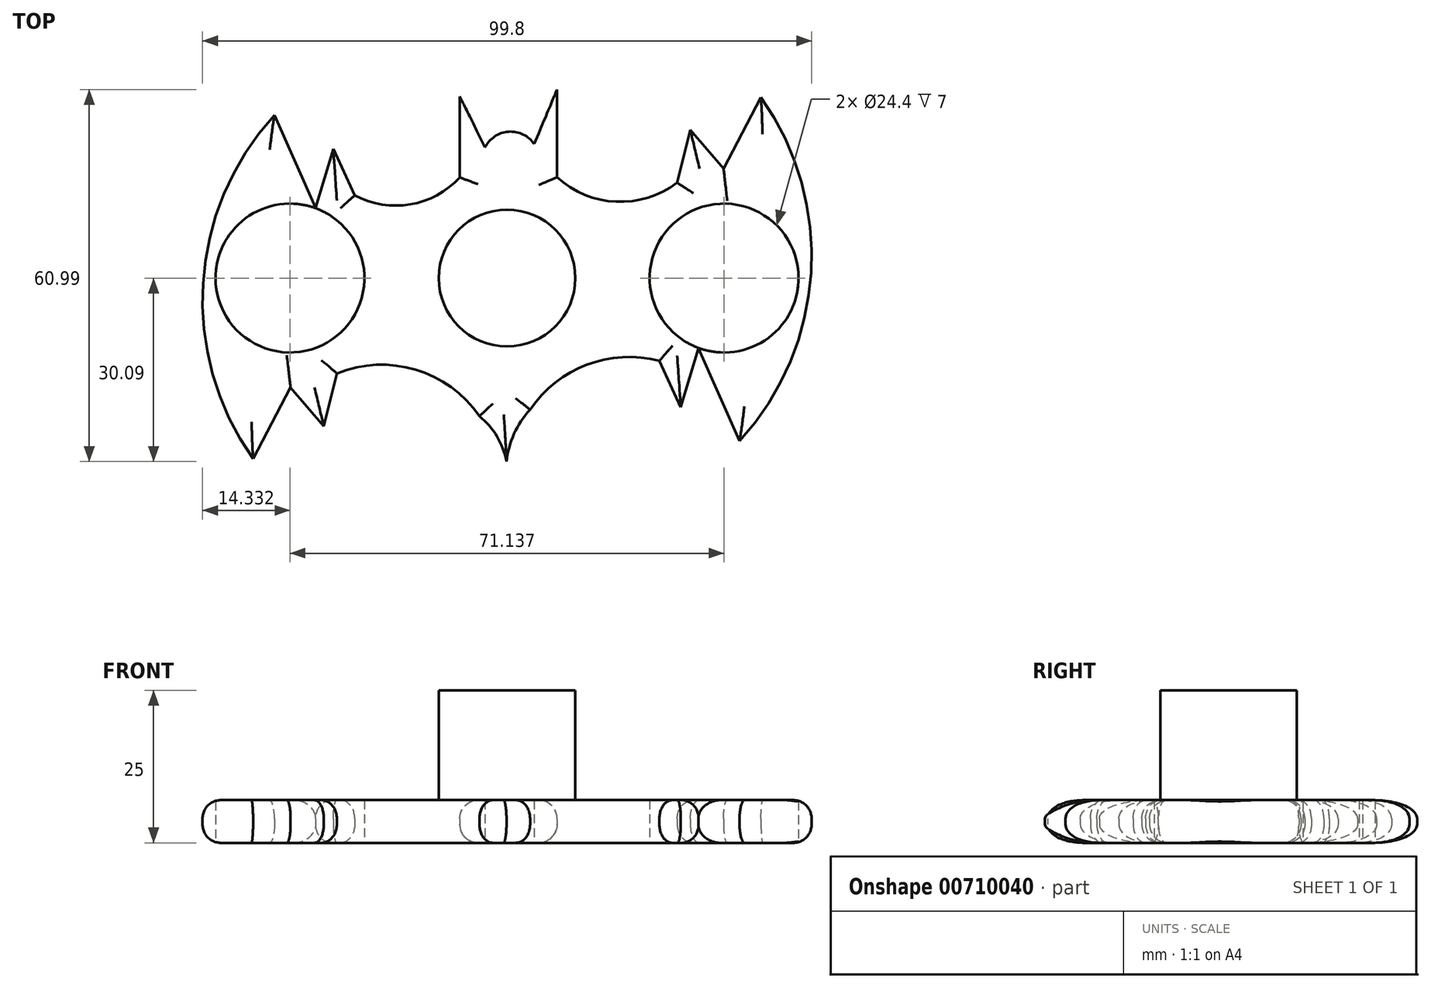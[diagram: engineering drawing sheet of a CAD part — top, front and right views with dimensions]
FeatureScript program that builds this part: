
annotation { "Feature Type Name" : "Feature", "Feature Type Description" : "" }
export const myFeature = defineFeature(function(context is Context, id is Id, definition is map)
    precondition{}
    {
        {
            var Q0;
            Q0=qCreatedBy(makeId("Top.planeOp"),FACE);
            var sketch = newSketch(context, id + "F0", { "sketchPlane" : qUnion([Q0])});
            skCircle(sketch, "E0", {"center": v(0, 0) * mm, "radius": 11.2 * mm});
            skCircle(sketch, "E1", {"center": v(0, 0) * mm, "radius": 13.2 * mm});
            skArc(sketch, "E2", {"start": v(-38.1, 26.72) * mm, "mid": v(-49.82, -0.84) * mm, "end": v(-41.61, -29.64) * mm});
            skArc(sketch, "E3.1.0", {"start": v(38.1, -26.72) * mm, "mid": v(49.82, 0.84) * mm, "end": v(41.61, 29.64) * mm});
            skLineSegment(sketch, "E4", {"start": v(-41.61, -29.64) * mm, "end": v(-35.48, -17.96) * mm});
            skLineSegment(sketch, "E5", {"start": v(-35.48, -17.96) * mm, "end": v(-35.48, -24.97) * mm});
            skArc(sketch, "E6", {"start": v(-4.53, -22.63) * mm, "mid": v(-14.98, -15.03) * mm, "end": v(-27.89, -15.62) * mm});
            skLineSegment(sketch, "E7.1.0", {"start": v(41.61, 29.64) * mm, "end": v(35.48, 17.96) * mm});
            skLineSegment(sketch, "E7.1.1", {"start": v(35.48, 17.96) * mm, "end": v(30.03, 24.29) * mm});
            skLineSegment(sketch, "E7.1.2", {"start": v(30.03, 24.29) * mm, "end": v(27.89, 15.62) * mm});
            skLineSegment(sketch, "E8", {"start": v(38.1, -26.72) * mm, "end": v(31.4, -11.53) * mm});
            skLineSegment(sketch, "E9", {"start": v(31.4, -11.53) * mm, "end": v(28.47, -21.17) * mm});
            skLineSegment(sketch, "E10", {"start": v(28.47, -21.17) * mm, "end": v(24.97, -13.58) * mm});
            skArc(sketch, "E11.1.0", {"start": v(-24.97, 13.58) * mm, "mid": v(-15.85, 12.08) * mm, "end": v(-7.74, 16.5) * mm});
            skLineSegment(sketch, "E11.1.2", {"start": v(-28.47, 21.17) * mm, "end": v(-24.97, 13.58) * mm});
            skLineSegment(sketch, "E11.1.4", {"start": v(-31.4, 11.53) * mm, "end": v(-28.47, 21.17) * mm});
            skLineSegment(sketch, "E11.1.5", {"start": v(-38.1, 26.72) * mm, "end": v(-31.4, 11.53) * mm});
            skArc(sketch, "E12", {"start": v(0, -34.06) * mm, "mid": v(-0.76, -27.75) * mm, "end": v(-4.53, -22.63) * mm});
            skArc(sketch, "E13.1.0", {"start": v(8.2, 16.53) * mm, "mid": v(17.88, 12.52) * mm, "end": v(27.89, 15.62) * mm});
            skLineSegment(sketch, "E14", {"start": v(-7.74, 16.5) * mm, "end": v(-7.74, 29.75) * mm});
            skLineSegment(sketch, "E15", {"start": v(-7.74, 29.75) * mm, "end": v(-3.6, 21.41) * mm});
            skLineSegment(sketch, "E16", {"start": v(8.2, 16.53) * mm, "end": v(8.2, 30.9) * mm});
            skLineSegment(sketch, "E17", {"start": v(8.2, 30.9) * mm, "end": v(4.45, 21.97) * mm});
            skArc(sketch, "E18", {"start": v(4.45, 21.97) * mm, "mid": v(0.27, 24) * mm, "end": v(-3.6, 21.41) * mm});
            skArc(sketch, "E19", {"start": v(24.97, -13.58) * mm, "mid": v(13.1, -14.2) * mm, "end": v(3.78, -21.57) * mm});
            skArc(sketch, "E20", {"start": v(3.78, -21.57) * mm, "mid": v(0.47, -27.38) * mm, "end": v(0, -34.06) * mm});
            skLineSegment(sketch, "E21.1.0", {"start": v(-35.48, -17.96) * mm, "end": v(-30.03, -24.29) * mm});
            skLineSegment(sketch, "E21.1.1", {"start": v(-30.03, -24.29) * mm, "end": v(-27.89, -15.62) * mm});
            skCircle(sketch, "E22", {"center": v(35.57, 0) * mm, "radius": 12.2 * mm});
            skCircle(sketch, "E23", {"center": v(-35.57, 0) * mm, "radius": 12.2 * mm});
            skSolve(sketch);
        }
        {
            var Q0;
            Q0=makeQuery(id+"F0.imprint","IMPRINT",FACE,{"disambiguationData":[TD([[makeQuery(id+"F0.imprint","IMPRINT",EDGE,{"derivedFrom":sQuery(id+"F0.wireOp",EDGE,"E0")}),-1.0]])]});
            var Q1;
            Q1=makeQuery(id+"F0.imprint","IMPRINT",FACE,{"disambiguationData":[TD([[makeQuery(id+"F0.imprint","IMPRINT",EDGE,{"derivedFrom":sQuery(id+"F0.wireOp",EDGE,"E1")}),-1.0]])]});
            extrude(context, id + "F1", {"entities" : qUnion([Q0, Q1]), "depth" : 7 * mm, "offsetDistance" : 25 * mm});
        }
        {
            var Q0;
            Q0=makeQuery(id+"F1.opExtrude","CAP_EDGE",EDGE,{"disambiguationData":[OSD([sQuery(id+"F0.wireOp",EDGE,"E20")])],"isStart":false});
            var Q1;
            Q1=makeQuery(id+"F1.opExtrude","CAP_EDGE",EDGE,{"disambiguationData":[OSD([sQuery(id+"F0.wireOp",EDGE,"E19")])],"isStart":false});
            var Q2;
            Q2=makeQuery(id+"F1.opExtrude","CAP_EDGE",EDGE,{"disambiguationData":[OSD([sQuery(id+"F0.wireOp",EDGE,"E9")])],"isStart":false});
            var Q3;
            Q3=makeQuery(id+"F1.opExtrude","CAP_EDGE",EDGE,{"disambiguationData":[OSD([sQuery(id+"F0.wireOp",EDGE,"E3.1.0")])],"isStart":false});
            var Q4;
            Q4=makeQuery(id+"F1.opExtrude","CAP_EDGE",EDGE,{"disambiguationData":[OSD([sQuery(id+"F0.wireOp",EDGE,"E8")])],"isStart":false});
            var Q5;
            Q5=makeQuery(id+"F1.opExtrude","CAP_EDGE",EDGE,{"disambiguationData":[OSD([sQuery(id+"F0.wireOp",EDGE,"E7.1.0")])],"isStart":false});
            var Q6;
            Q6=makeQuery(id+"F1.opExtrude","CAP_EDGE",EDGE,{"disambiguationData":[OSD([sQuery(id+"F0.wireOp",EDGE,"E7.1.1")])],"isStart":false});
            var Q7;
            Q7=makeQuery(id+"F1.opExtrude","CAP_EDGE",EDGE,{"disambiguationData":[OSD([sQuery(id+"F0.wireOp",EDGE,"E7.1.2")])],"isStart":false});
            var Q8;
            Q8=makeQuery(id+"F1.opExtrude","CAP_EDGE",EDGE,{"disambiguationData":[OSD([sQuery(id+"F0.wireOp",EDGE,"E13.1.0")])],"isStart":false});
            var Q9;
            Q9=makeQuery(id+"F1.opExtrude","CAP_EDGE",EDGE,{"disambiguationData":[OSD([sQuery(id+"F0.wireOp",EDGE,"E16")])],"isStart":false});
            var Q10;
            Q10=makeQuery(id+"F1.opExtrude","CAP_EDGE",EDGE,{"disambiguationData":[OSD([sQuery(id+"F0.wireOp",EDGE,"E14")])],"isStart":false});
            var Q11;
            Q11=makeQuery(id+"F1.opExtrude","CAP_EDGE",EDGE,{"disambiguationData":[OSD([sQuery(id+"F0.wireOp",EDGE,"E11.1.0")])],"isStart":false});
            var Q12;
            Q12=makeQuery(id+"F1.opExtrude","CAP_EDGE",EDGE,{"disambiguationData":[OSD([sQuery(id+"F0.wireOp",EDGE,"E11.1.2")])],"isStart":false});
            var Q13;
            Q13=makeQuery(id+"F1.opExtrude","CAP_EDGE",EDGE,{"disambiguationData":[OSD([sQuery(id+"F0.wireOp",EDGE,"E11.1.5")])],"isStart":false});
            var Q14;
            Q14=makeQuery(id+"F1.opExtrude","CAP_EDGE",EDGE,{"disambiguationData":[OSD([sQuery(id+"F0.wireOp",EDGE,"E11.1.4")])],"isStart":false});
            var Q15;
            Q15=makeQuery(id+"F1.opExtrude","CAP_EDGE",EDGE,{"disambiguationData":[OSD([sQuery(id+"F0.wireOp",EDGE,"E2")])],"isStart":false});
            var Q16;
            Q16=makeQuery(id+"F1.opExtrude","CAP_EDGE",EDGE,{"disambiguationData":[OSD([sQuery(id+"F0.wireOp",EDGE,"E4")])],"isStart":false});
            var Q17;
            Q17=makeQuery(id+"F1.opExtrude","CAP_EDGE",EDGE,{"disambiguationData":[OSD([sQuery(id+"F0.wireOp",EDGE,"wEF84jsq-XExs-cQrN-D3yr-Ib7uIkRzdJAm")])],"isStart":false});
            var Q18;
            Q18=makeQuery(id+"F1.opExtrude","CAP_EDGE",EDGE,{"disambiguationData":[OSD([sQuery(id+"F0.wireOp",EDGE,"E12")])],"isStart":false});
            var Q19;
            Q19=makeQuery(id+"F1.opExtrude","CAP_EDGE",EDGE,{"disambiguationData":[OSD([sQuery(id+"F0.wireOp",EDGE,"E5")])],"isStart":false});
            var Q20;
            Q20=makeQuery(id+"F1.opExtrude","CAP_EDGE",EDGE,{"disambiguationData":[OSD([sQuery(id+"F0.wireOp",EDGE,"E10")])],"isStart":false});
            var Q21;
            Q21=makeQuery(id+"F1.opExtrude","CAP_EDGE",EDGE,{"disambiguationData":[OSD([sQuery(id+"F0.wireOp",EDGE,"E21.1.1")])],"isStart":false});
            var Q22;
            Q22=makeQuery(id+"F1.opExtrude","CAP_EDGE",EDGE,{"disambiguationData":[OSD([sQuery(id+"F0.wireOp",EDGE,"E6")])],"isStart":false});
            var Q23;
            Q23=makeQuery(id+"F1.opExtrude","CAP_EDGE",EDGE,{"disambiguationData":[OSD([sQuery(id+"F0.wireOp",EDGE,"E21.1.0")])],"isStart":false});
            var Q24;
            Q24=makeQuery(id+"F1.opExtrude","CAP_EDGE",EDGE,{"disambiguationData":[OSD([sQuery(id+"F0.wireOp",EDGE,"E3.1.0")])],"isStart":true});
            var Q25;
            Q25=makeQuery(id+"F1.opExtrude","CAP_EDGE",EDGE,{"disambiguationData":[OSD([sQuery(id+"F0.wireOp",EDGE,"E8")])],"isStart":true});
            var Q26;
            Q26=makeQuery(id+"F1.opExtrude","CAP_EDGE",EDGE,{"disambiguationData":[OSD([sQuery(id+"F0.wireOp",EDGE,"E9")])],"isStart":true});
            var Q27;
            Q27=makeQuery(id+"F1.opExtrude","CAP_EDGE",EDGE,{"disambiguationData":[OSD([sQuery(id+"F0.wireOp",EDGE,"E10")])],"isStart":true});
            var Q28;
            Q28=makeQuery(id+"F1.opExtrude","CAP_EDGE",EDGE,{"disambiguationData":[OSD([sQuery(id+"F0.wireOp",EDGE,"E19")])],"isStart":true});
            var Q29;
            Q29=makeQuery(id+"F1.opExtrude","CAP_EDGE",EDGE,{"disambiguationData":[OSD([sQuery(id+"F0.wireOp",EDGE,"E6")])],"isStart":true});
            var Q30;
            Q30=makeQuery(id+"F1.opExtrude","CAP_EDGE",EDGE,{"disambiguationData":[OSD([sQuery(id+"F0.wireOp",EDGE,"E12")])],"isStart":true});
            var Q31;
            Q31=makeQuery(id+"F1.opExtrude","CAP_EDGE",EDGE,{"disambiguationData":[OSD([sQuery(id+"F0.wireOp",EDGE,"E20")])],"isStart":true});
            var Q32;
            Q32=makeQuery(id+"F1.opExtrude","CAP_EDGE",EDGE,{"disambiguationData":[OSD([sQuery(id+"F0.wireOp",EDGE,"E21.1.1")])],"isStart":true});
            var Q33;
            Q33=makeQuery(id+"F1.opExtrude","CAP_EDGE",EDGE,{"disambiguationData":[OSD([sQuery(id+"F0.wireOp",EDGE,"E21.1.0")])],"isStart":true});
            var Q34;
            Q34=makeQuery(id+"F1.opExtrude","CAP_EDGE",EDGE,{"disambiguationData":[OSD([sQuery(id+"F0.wireOp",EDGE,"E4")])],"isStart":true});
            var Q35;
            Q35=makeQuery(id+"F1.opExtrude","CAP_EDGE",EDGE,{"disambiguationData":[OSD([sQuery(id+"F0.wireOp",EDGE,"E2")])],"isStart":true});
            var Q36;
            Q36=makeQuery(id+"F1.opExtrude","CAP_EDGE",EDGE,{"disambiguationData":[OSD([sQuery(id+"F0.wireOp",EDGE,"E11.1.5")])],"isStart":true});
            var Q37;
            Q37=makeQuery(id+"F1.opExtrude","CAP_EDGE",EDGE,{"disambiguationData":[OSD([sQuery(id+"F0.wireOp",EDGE,"E11.1.4")])],"isStart":true});
            var Q38;
            Q38=makeQuery(id+"F1.opExtrude","CAP_EDGE",EDGE,{"disambiguationData":[OSD([sQuery(id+"F0.wireOp",EDGE,"E14")])],"isStart":true});
            var Q39;
            Q39=makeQuery(id+"F1.opExtrude","CAP_EDGE",EDGE,{"disambiguationData":[OSD([sQuery(id+"F0.wireOp",EDGE,"E16")])],"isStart":true});
            var Q40;
            Q40=makeQuery(id+"F1.opExtrude","CAP_EDGE",EDGE,{"disambiguationData":[OSD([sQuery(id+"F0.wireOp",EDGE,"E13.1.0")])],"isStart":true});
            var Q41;
            Q41=makeQuery(id+"F1.opExtrude","CAP_EDGE",EDGE,{"disambiguationData":[OSD([sQuery(id+"F0.wireOp",EDGE,"E7.1.2")])],"isStart":true});
            var Q42;
            Q42=makeQuery(id+"F1.opExtrude","CAP_EDGE",EDGE,{"disambiguationData":[OSD([sQuery(id+"F0.wireOp",EDGE,"E7.1.1")])],"isStart":true});
            var Q43;
            Q43=makeQuery(id+"F1.opExtrude","CAP_EDGE",EDGE,{"disambiguationData":[OSD([sQuery(id+"F0.wireOp",EDGE,"E7.1.0")])],"isStart":true});
            var Q44;
            Q44=makeQuery(id+"F1.opExtrude","CAP_EDGE",EDGE,{"disambiguationData":[OSD([sQuery(id+"F0.wireOp",EDGE,"E11.1.0")])],"isStart":true});
            var Q45;
            Q45=makeQuery(id+"F1.opExtrude","CAP_EDGE",EDGE,{"disambiguationData":[OSD([sQuery(id+"F0.wireOp",EDGE,"E11.1.2")])],"isStart":true});
            fillet(context, id + "F2", {"entities" : qUnion([Q0, Q1, Q2, Q3, Q4, Q5, Q6, Q7, Q8, Q9, Q10, Q11, Q12, Q13, Q14, Q15, Q16, Q17, Q18, Q19, Q20, Q21, Q22, Q23, Q24, Q25, Q26, Q27, Q28, Q29, Q30, Q31, Q32, Q33, Q34, Q35, Q36, Q37, Q38, Q39, Q40, Q41, Q42, Q43, Q44, Q45]), "radius" : 3 * mm, "tangentPropagation" : true, "allowEdgeOverflow" : false});
        }
        {
            var Q0;
            Q0=qCreatedBy(makeId("Top.planeOp"),FACE);
            var sketch = newSketch(context, id + "F3", { "sketchPlane" : qUnion([Q0])});
            skCircle(sketch, "E24", {"center": v(0, 0) * mm, "radius": 11.2 * mm});
            skSolve(sketch);
        }
        {
            var Q0;
            Q0 = qSketchRegion(id + "F3", true);
            extrude(context, id + "F4", {"entities" : qUnion([Q0]), "operationType" : NewBodyOperationType.ADD, "depth" : 25 * mm, "offsetDistance" : 25 * mm});
        }
    });
